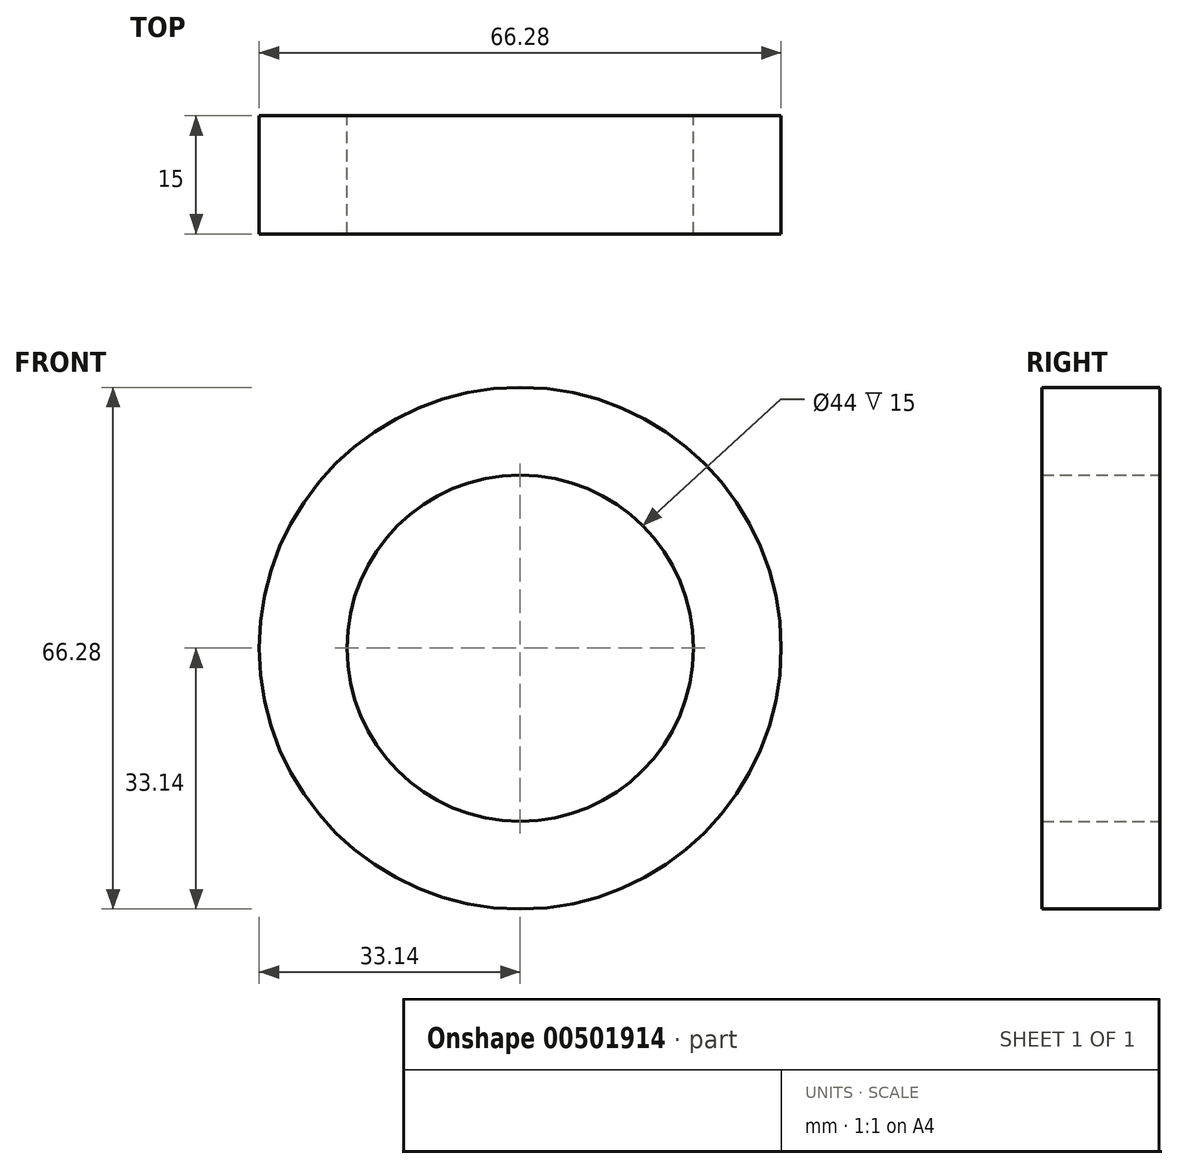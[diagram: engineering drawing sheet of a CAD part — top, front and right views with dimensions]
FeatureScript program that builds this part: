
annotation { "Feature Type Name" : "Feature", "Feature Type Description" : "" }
export const myFeature = defineFeature(function(context is Context, id is Id, definition is map)
    precondition{}
    {
        {
            var Q0;
            Q0=qCreatedBy(makeId("Front.planeOp"),FACE);
            var sketch = newSketch(context, id + "F0", { "sketchPlane" : qUnion([Q0])});
            skCircle(sketch, "E0", {"center": v(0, 0) * mm, "radius": 22 * mm});
            skCircle(sketch, "E1", {"center": v(0, 0) * mm, "radius": 33.14 * mm});
            skSolve(sketch);
        }
        {
            var Q0;
            Q0=makeQuery(id+"F0.imprint","IMPRINT",FACE,{"disambiguationData":[TD([[makeQuery(id+"F0.imprint","IMPRINT",EDGE,{"derivedFrom":sQuery(id+"F0.wireOp",EDGE,"E0")}),1.0]])]});
            var sketch = newSketch(context, id + "F1", { "sketchPlane" : qUnion([Q0])});
            skSolve(sketch);
        }
        {
            var Q0;
            Q0=makeQuery(id+"F0.imprint","IMPRINT",FACE,{"disambiguationData":[TD([[makeQuery(id+"F0.imprint","IMPRINT",EDGE,{"derivedFrom":sQuery(id+"F0.wireOp",EDGE,"E0")}),-1.0]])]});
            var Q1;
            Q1=makeQuery(id+"F1.imprint","IMPRINT",FACE,{"disambiguationData":[TD([[makeQuery(id+"F1.imprint","IMPRINT",EDGE,{"derivedFrom":makeQuery(id+"F0.imprint","IMPRINT",EDGE,{"derivedFrom":sQuery(id+"F0.wireOp",EDGE,"E0")})}),1.0]])]});
            extrude(context, id + "F2", {"entities" : qUnion([Q0, Q1]), "depth" : 15 * mm});
        }
    });
